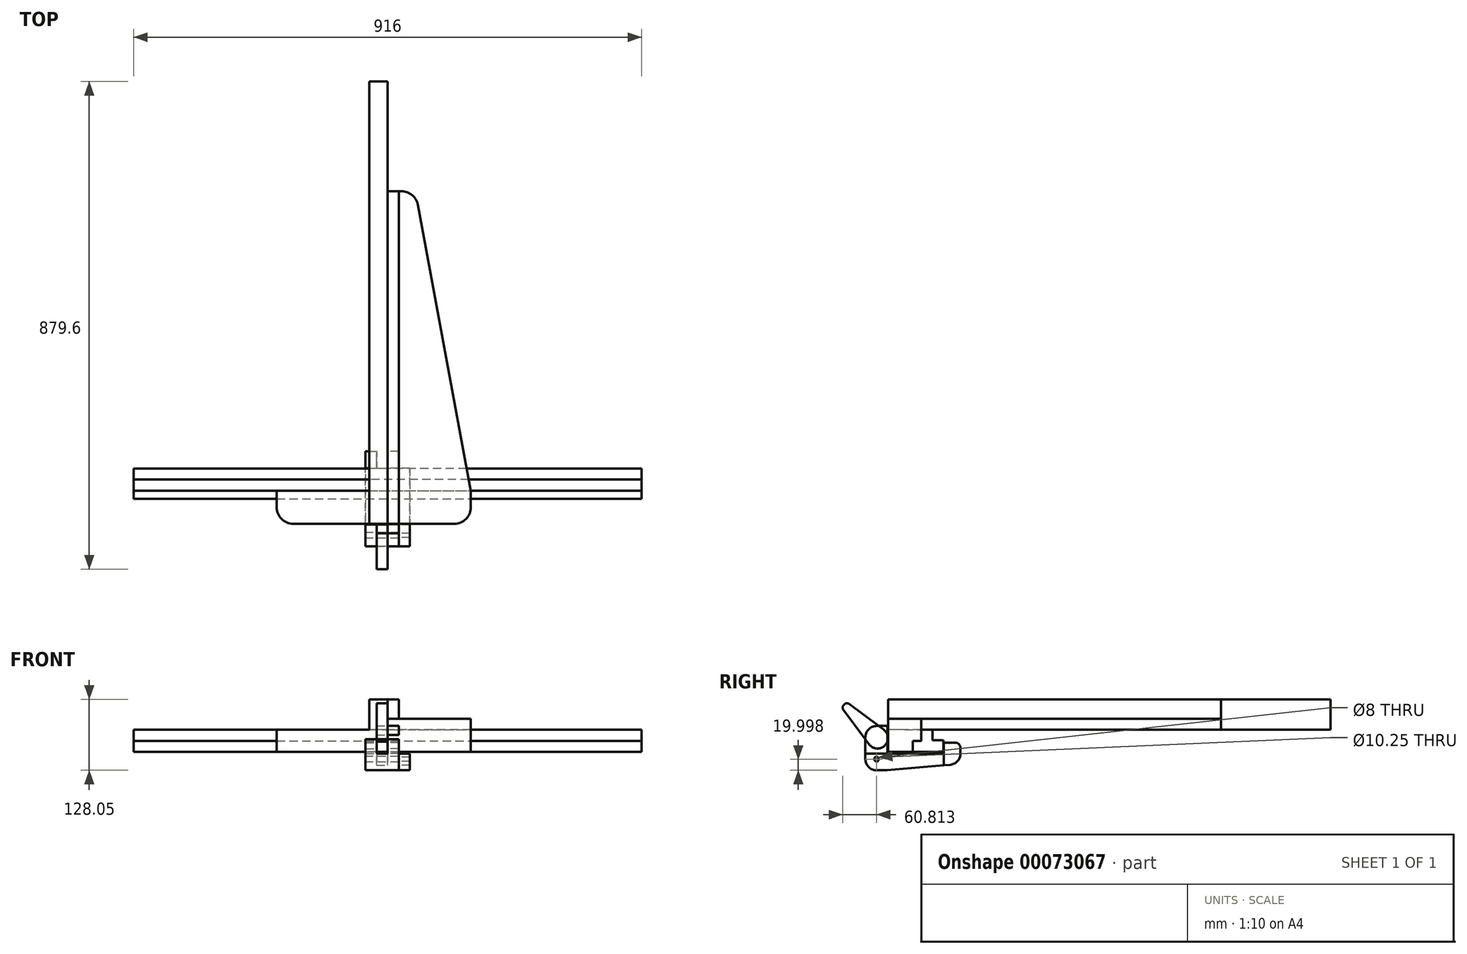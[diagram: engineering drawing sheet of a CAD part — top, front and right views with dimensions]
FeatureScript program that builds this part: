
annotation { "Feature Type Name" : "Feature", "Feature Type Description" : "" }
export const myFeature = defineFeature(function(context is Context, id is Id, definition is map)
    precondition{}
    {
        {
            var Q0;
            Q0=qCreatedBy(makeId("Front.planeOp"),FACE);
            var sketch = newSketch(context, id + "F0", { "sketchPlane" : qUnion([Q0])});
            skLineSegment(sketch, "E0.bottom", {"start": v(0, 0) * mm, "end": v(-33, 0) * mm});
            skLineSegment(sketch, "E0.top", {"start": v(0, 55) * mm, "end": v(-33, 55) * mm});
            skLineSegment(sketch, "E0.left", {"start": v(0, 0) * mm, "end": v(0, 55) * mm});
            skLineSegment(sketch, "E0.right", {"start": v(-33, 0) * mm, "end": v(-33, 55) * mm});
            skLineSegment(sketch, "E1.bottom", {"start": v(0, 20) * mm, "end": v(20, 20) * mm});
            skLineSegment(sketch, "E1.top", {"start": v(0, 55) * mm, "end": v(20, 55) * mm});
            skLineSegment(sketch, "E1.left", {"start": v(0, 20) * mm, "end": v(0, 55) * mm});
            skLineSegment(sketch, "E1.right", {"start": v(20, 20) * mm, "end": v(20, 55) * mm});
            skSolve(sketch);
        }
        {
            var Q0;
            Q0=makeQuery(id+"F0.imprint","IMPRINT",FACE,{"disambiguationData":[TD([[makeQuery(id+"F0.imprint","IMPRINT",EDGE,{"derivedFrom":sQuery(id+"F0.wireOp",EDGE,"E0.bottom")}),-1.0]])]});
            extrude(context, id + "F1", {"entities" : qUnion([Q0]), "oppositeDirection" : true, "depth" : 798 * mm});
        }
        {
            var Q0;
            Q0=qCreatedBy(makeId("Top.planeOp"),FACE);
            var sketch = newSketch(context, id + "F2", { "sketchPlane" : qUnion([Q0])});
            skLineSegment(sketch, "E2", {"start": v(0, 0) * mm, "end": v(0, 600) * mm});
            skLineSegment(sketch, "E3", {"start": v(0, 600) * mm, "end": v(25.05, 600) * mm});
            skLineSegment(sketch, "E4", {"start": v(120, 0) * mm, "end": v(0, 0) * mm});
            skLineSegment(sketch, "E5", {"start": v(0, 0) * mm, "end": v(-170, 0) * mm});
            skLineSegment(sketch, "E6", {"start": v(-200, 30) * mm, "end": v(-200, 60) * mm});
            skLineSegment(sketch, "E7", {"start": v(-200, 60) * mm, "end": v(150, 60) * mm});
            skLineSegment(sketch, "E8", {"start": v(150, 60) * mm, "end": v(150, 30) * mm});
            skLineSegment(sketch, "E9", {"start": v(54.54, 575.46) * mm, "end": v(150, 60) * mm});
            skPoint(sketch, "E10.visualSharp", {"position": v(-200, 0) * mm});
            skArc(sketch, "E10.filletArc", {"start": v(-200, 30) * mm, "mid": v(-191.21, 8.79) * mm, "end": v(-170, 0) * mm});
            skPoint(sketch, "E11.visualSharp", {"position": v(150, 0) * mm});
            skArc(sketch, "E11.filletArc", {"start": v(120, 0) * mm, "mid": v(141.21, 8.79) * mm, "end": v(150, 30) * mm});
            skPoint(sketch, "E12.visualSharp", {"position": v(50, 600) * mm});
            skArc(sketch, "E12.filletArc", {"start": v(54.54, 575.46) * mm, "mid": v(44.23, 593.06) * mm, "end": v(25.05, 600) * mm});
            skLineSegment(sketch, "E13", {"start": v(-200, 45) * mm, "end": v(150, 45) * mm});
            skSolve(sketch);
        }
        {
            var Q0;
            {var subQ4=sQuery(id+"F2.wireOp",EDGE,"E3");Q0=makeQuery(id+"F2.imprint","IMPRINT",FACE,{"disambiguationData":[TD([[makeQuery(id+"F2.imprint","IMPRINT",EDGE,{"derivedFrom":subQ4}),-1.0]])]});}
            var Q1;
            {var subQ4=sQuery(id+"F2.wireOp",EDGE,"E4");Q1=makeQuery(id+"F2.imprint","IMPRINT",FACE,{"disambiguationData":[TD([[makeQuery(id+"F2.imprint","IMPRINT",EDGE,{"derivedFrom":subQ4}),-1.0]])]});}
            var Q2;
            {var subQ0=sQuery(id+"F2.wireOp",EDGE,"E7");var subQ1=sQuery(id+"F2.wireOp",EDGE,"E2");var subQ2=makeQuery(id+"F2.imprint","INTERSECT",VERTEX,{"derivedFrom":[subQ1,subQ0]});Q2=makeQuery(id+"F2.imprint","IMPRINT",FACE,{"disambiguationData":[TD([[makeQuery(id+"F2.imprint","IMPRINT",EDGE,{"disambiguationData":[TD([[subQ2,1.0]])],"derivedFrom":subQ1}),-1.0]])]});}
            extrude(context, id + "F3", {"entities" : qUnion([Q0, Q1, Q2]), "depth" : 20 * mm});
        }
        {
            var Q0;
            Q0=makeQuery(id+"F0.imprint","IMPRINT",FACE,{"disambiguationData":[TD([[makeQuery(id+"F0.imprint","IMPRINT",EDGE,{"derivedFrom":sQuery(id+"F0.wireOp",EDGE,"E1.bottom")}),1.0]])]});
            var Q1;
            Q1=makeQuery(id+"F3.opExtrude","SWEPT_FACE",FACE,{"disambiguationData":[OSD([sQuery(id+"F2.wireOp",EDGE,"E3")])]});
            extrude(context, id + "F4", {"entities" : qUnion([Q0]), "endBound" : BoundingType.UP_TO_SURFACE, "oppositeDirection" : true, "endBoundEntityFace" : qUnion([Q1]), "depth" : 559.37 * mm});
        }
        {
            var Q0;
            {var subQ4=sQuery(id+"F2.wireOp",EDGE,"E4");Q0=makeQuery(id+"F2.imprint","IMPRINT",FACE,{"disambiguationData":[TD([[makeQuery(id+"F2.imprint","IMPRINT",EDGE,{"derivedFrom":subQ4}),-1.0]])]});}
            var Q1;
            {var subQ4=sQuery(id+"F2.wireOp",EDGE,"E5");Q1=makeQuery(id+"F2.imprint","IMPRINT",FACE,{"disambiguationData":[TD([[makeQuery(id+"F2.imprint","IMPRINT",EDGE,{"derivedFrom":subQ4}),-1.0]])]});}
            var Q2;
            {var subQ0=sQuery(id+"F2.wireOp",EDGE,"E7");var subQ1=sQuery(id+"F2.wireOp",EDGE,"E2");var subQ2=makeQuery(id+"F2.imprint","INTERSECT",VERTEX,{"derivedFrom":[subQ1,subQ0]});Q2=makeQuery(id+"F2.imprint","IMPRINT",FACE,{"disambiguationData":[TD([[makeQuery(id+"F2.imprint","IMPRINT",EDGE,{"disambiguationData":[TD([[subQ2,1.0]])],"derivedFrom":subQ1}),1.0]])]});}
            var Q3;
            {var subQ0=sQuery(id+"F2.wireOp",EDGE,"E7");var subQ1=sQuery(id+"F2.wireOp",EDGE,"E2");var subQ2=makeQuery(id+"F2.imprint","INTERSECT",VERTEX,{"derivedFrom":[subQ1,subQ0]});Q3=makeQuery(id+"F2.imprint","IMPRINT",FACE,{"disambiguationData":[TD([[makeQuery(id+"F2.imprint","IMPRINT",EDGE,{"disambiguationData":[TD([[subQ2,1.0]])],"derivedFrom":subQ1}),-1.0]])]});}
            extrude(context, id + "F5", {"entities" : qUnion([Q0, Q1, Q2, Q3]), "oppositeDirection" : true, "depth" : 20 * mm});
        }
        {
            var Q0;
            {var subQ4=sQuery(id+"F2.wireOp",EDGE,"E5");Q0=makeQuery(id+"F2.imprint","IMPRINT",FACE,{"disambiguationData":[TD([[makeQuery(id+"F2.imprint","IMPRINT",EDGE,{"derivedFrom":subQ4}),-1.0]])]});}
            var Q1;
            {var subQ1=sQuery(id+"F2.wireOp",EDGE,"E4");Q1=makeQuery(id+"F2.imprint","IMPRINT",FACE,{"disambiguationData":[TD([[makeQuery(id+"F2.imprint","IMPRINT",EDGE,{"derivedFrom":subQ1}),-1.0]])]});}
            extrude(context, id + "F6", {"entities" : qUnion([Q0, Q1]), "operationType" : NewBodyOperationType.ADD, "oppositeDirection" : true, "depth" : 40 * mm});
        }
        {
            var Q0;
            Q0=qCreatedBy(makeId("Right.planeOp"),FACE);
            var sketch = newSketch(context, id + "F7", { "sketchPlane" : qUnion([Q0])});
            skLineSegment(sketch, "E14", {"start": v(45, -20) * mm, "end": v(45, -40) * mm});
            skLineSegment(sketch, "E15", {"start": v(60, -20) * mm, "end": v(45, -20) * mm});
            skLineSegment(sketch, "E16", {"start": v(60, 0) * mm, "end": v(60, -20) * mm});
            skLineSegment(sketch, "E17", {"start": v(45, -40) * mm, "end": v(100, -40) * mm});
            skLineSegment(sketch, "E18", {"start": v(80, 0) * mm, "end": v(60, 0) * mm});
            skLineSegment(sketch, "E19", {"start": v(100, -40) * mm, "end": v(100, -19) * mm});
            skLineSegment(sketch, "E20", {"start": v(100, -19) * mm, "end": v(80, -19) * mm});
            skLineSegment(sketch, "E21", {"start": v(80, -19) * mm, "end": v(80, 0) * mm});
            skLineSegment(sketch, "E22", {"start": v(-1.29, -43.05) * mm, "end": v(100.71, -43.05) * mm});
            skLineSegment(sketch, "E23", {"start": v(100.71, -43.05) * mm, "end": v(100.71, -23.05) * mm});
            skLineSegment(sketch, "E24", {"start": v(100.71, -23.05) * mm, "end": v(120.71, -23.05) * mm});
            skLineSegment(sketch, "E25", {"start": v(130.71, -33.05) * mm, "end": v(130.71, -43.05) * mm});
            skLineSegment(sketch, "E26", {"start": v(112.47, -62.97) * mm, "end": v(-1.79, -73.05) * mm});
            skLineSegment(sketch, "E27", {"start": v(-1.79, -73.05) * mm, "end": v(-20.79, -73.05) * mm});
            skLineSegment(sketch, "E28", {"start": v(-40.79, -53.05) * mm, "end": v(-40.79, -13.05) * mm});
            skLineSegment(sketch, "E29", {"start": v(-20.79, 6.95) * mm, "end": v(-0.79, 6.95) * mm});
            skPoint(sketch, "E30.visualSharp", {"position": v(-40.79, -73.05) * mm});
            skArc(sketch, "E30.filletArc", {"start": v(-40.79, -53.05) * mm, "mid": v(-34.93, -67.2) * mm, "end": v(-20.79, -73.05) * mm});
            skPoint(sketch, "E31.visualSharp", {"position": v(130.71, -61.37) * mm});
            skArc(sketch, "E31.filletArc", {"start": v(112.47, -62.97) * mm, "mid": v(125.46, -56.56) * mm, "end": v(130.71, -43.05) * mm});
            skLineSegment(sketch, "E32", {"start": v(-0.79, 6.95) * mm, "end": v(-1.29, -43.05) * mm});
            skPoint(sketch, "E33.visualSharp", {"position": v(-40.79, 6.95) * mm});
            skArc(sketch, "E33.filletArc", {"start": v(-20.79, 6.95) * mm, "mid": v(-34.93, 1.1) * mm, "end": v(-40.79, -13.05) * mm});
            skPoint(sketch, "E34.visualSharp", {"position": v(130.71, -23.05) * mm});
            skArc(sketch, "E34.filletArc", {"start": v(130.71, -33.05) * mm, "mid": v(127.78, -25.98) * mm, "end": v(120.71, -23.05) * mm});
            skLineSegment(sketch, "E35", {"start": v(-1.29, -43.05) * mm, "end": v(-40.79, -43.05) * mm});
            skCircle(sketch, "E36", {"center": v(-20.79, -13.05) * mm, "radius": 4 * mm});
            skArc(sketch, "E37", {"start": v(-33.78, -26.3) * mm, "mid": v(-5.53, -28.31) * mm, "end": v(-7.53, -0.06) * mm});
            skLineSegment(sketch, "E38", {"start": v(-18.79, -15.05) * mm, "end": v(-40.79, 6.95) * mm, "construction": true});
            skLineSegment(sketch, "E39", {"start": v(-69.15, 46.2) * mm, "end": v(-7.53, -0.06) * mm});
            skLineSegment(sketch, "E40.MirrorCS", {"start": v(-80.04, 35.31) * mm, "end": v(-33.78, -26.3) * mm});
            skArc(sketch, "E41", {"start": v(-69.15, 46.2) * mm, "mid": v(-79.32, 45.48) * mm, "end": v(-80.04, 35.31) * mm});
            skLineSegment(sketch, "E42", {"start": v(100.71, -43.05) * mm, "end": v(100.71, -64.01) * mm});
            skCircle(sketch, "E43", {"center": v(-20.79, -53.05) * mm, "radius": 4 * mm});
            skCircle(sketch, "E44", {"center": v(-20.79, -53.05) * mm, "radius": 5.12 * mm});
            skSolve(sketch);
        }
        {
            var Q0;
            Q0=makeQuery(id+"F7.imprint","IMPRINT",FACE,{"disambiguationData":[TD([[makeQuery(id+"F7.imprint","IMPRINT",EDGE,{"derivedFrom":sQuery(id+"F7.wireOp",EDGE,"E14")}),1.0]])]});
            extrude(context, id + "F8", {"entities" : qUnion([Q0]), "depth" : 458 * mm, "hasSecondDirection" : true, "secondDirectionOppositeDirection" : true, "secondDirectionDepth" : 458 * mm});
        }
        {
            var Q0;
            Q0=makeQuery(id+"F7.imprint","IMPRINT",FACE,{"disambiguationData":[TD([[makeQuery(id+"F7.imprint","IMPRINT",EDGE,{"derivedFrom":sQuery(id+"F7.wireOp",EDGE,"E22")}),-1.0]])]});
            var Q1;
            Q1=makeQuery(id+"F7.imprint","IMPRINT",FACE,{"disambiguationData":[TD([[makeQuery(id+"F7.imprint","IMPRINT",EDGE,{"derivedFrom":sQuery(id+"F7.wireOp",EDGE,"E29")}),-1.0]])]});
            var Q2;
            Q2=makeQuery(id+"F7.imprint","IMPRINT",FACE,{"disambiguationData":[TD([[makeQuery(id+"F7.imprint","IMPRINT",EDGE,{"derivedFrom":sQuery(id+"F7.wireOp",EDGE,"E36")}),-1.0]])]});
            var Q3;
            Q3=makeQuery(id+"F7.imprint","IMPRINT",FACE,{"disambiguationData":[TD([[makeQuery(id+"F7.imprint","IMPRINT",EDGE,{"derivedFrom":sQuery(id+"F7.wireOp",EDGE,"E23")}),-1.0]])]});
            var Q4;
            {var subQ5=sQuery(id+"F7.wireOp",EDGE,"E35");Q4=makeQuery(id+"F7.imprint","IMPRINT",FACE,{"disambiguationData":[TD([[makeQuery(id+"F7.imprint","IMPRINT",EDGE,{"derivedFrom":subQ5}),-1.0]])]});}
            extrude(context, id + "F9", {"entities" : qUnion([Q0, Q1, Q2, Q3, Q4]), "depth" : 20 * mm});
        }
        {
            var Q0;
            Q0=makeQuery(id+"F7.imprint","IMPRINT",FACE,{"disambiguationData":[TD([[makeQuery(id+"F7.imprint","IMPRINT",EDGE,{"derivedFrom":sQuery(id+"F7.wireOp",EDGE,"E22")}),-1.0]])]});
            extrude(context, id + "F10", {"entities" : qUnion([Q0]), "operationType" : NewBodyOperationType.ADD, "oppositeDirection" : true, "depth" : 20 * mm});
        }
        {
            var Q0;
            Q0=makeQuery(id+"F9.opExtrude","CAP_FACE",FACE,{"disambiguationData":[OSD([sQuery(id+"F7.wireOp",EDGE,"E22"),sQuery(id+"F7.wireOp",EDGE,"E23"),sQuery(id+"F7.wireOp",EDGE,"E24"),sQuery(id+"F7.wireOp",EDGE,"E25"),sQuery(id+"F7.wireOp",EDGE,"E26"),sQuery(id+"F7.wireOp",EDGE,"E27"),sQuery(id+"F7.wireOp",EDGE,"E28"),sQuery(id+"F7.wireOp",EDGE,"E29"),sQuery(id+"F7.wireOp",EDGE,"E30.filletArc"),sQuery(id+"F7.wireOp",EDGE,"E31.filletArc"),sQuery(id+"F7.wireOp",EDGE,"E32"),sQuery(id+"F7.wireOp",EDGE,"E33.filletArc"),sQuery(id+"F7.wireOp",EDGE,"E34.filletArc")])],"isStart":false});
            extrude(context, id + "F11", {"entities" : qUnion([Q0]), "operationType" : NewBodyOperationType.ADD, "oppositeDirection" : true, "depth" : 60 * mm, "hasSecondDirection" : true, "secondDirectionOppositeDirection" : true, "secondDirectionDepth" : 40 * mm});
        }
        {
            var Q0;
            Q0=makeQuery(id+"F7.imprint","IMPRINT",FACE,{"disambiguationData":[TD([[makeQuery(id+"F7.imprint","IMPRINT",EDGE,{"derivedFrom":sQuery(id+"F7.wireOp",EDGE,"E36")}),-1.0]])]});
            var Q1;
            {var subQ5=sQuery(id+"F7.wireOp",EDGE,"E41");Q1=makeQuery(id+"F7.imprint","IMPRINT",FACE,{"disambiguationData":[TD([[makeQuery(id+"F7.imprint","IMPRINT",EDGE,{"derivedFrom":subQ5}),1.0]])]});}
            var Q2;
            {var subQ0=sQuery(id+"F7.wireOp",EDGE,"E37");var subQ1=sQuery(id+"F7.wireOp",EDGE,"E32");var subQ2=makeQuery(id+"F7.imprint","INTERSECT",VERTEX,{"disambiguationData":[OD(0.0)],"derivedFrom":[subQ1,subQ0]});Q2=makeQuery(id+"F7.imprint","IMPRINT",FACE,{"disambiguationData":[TD([[makeQuery(id+"F7.imprint","IMPRINT",EDGE,{"disambiguationData":[TD([[subQ2,-1.0]])],"derivedFrom":subQ1}),1.0]])]});}
            extrude(context, id + "F12", {"entities" : qUnion([Q0, Q1, Q2]), "oppositeDirection" : true, "depth" : 20 * mm});
        }
        {
            var Q0;
            Q0=makeQuery(id+"F7.imprint","IMPRINT",FACE,{"disambiguationData":[TD([[makeQuery(id+"F7.imprint","IMPRINT",EDGE,{"derivedFrom":sQuery(id+"F7.wireOp",EDGE,"E22")}),-1.0]])]});
            var Q1;
            Q1=makeQuery(id+"F7.imprint","IMPRINT",FACE,{"disambiguationData":[TD([[makeQuery(id+"F7.imprint","IMPRINT",EDGE,{"derivedFrom":sQuery(id+"F7.wireOp",EDGE,"E43")}),-1.0]])]});
            extrude(context, id + "F13", {"entities" : qUnion([Q0, Q1]), "depth" : 40 * mm, "hasSecondDirection" : true, "secondDirectionOppositeDirection" : false, "secondDirectionDepth" : 20.5 * mm});
        }
    });
